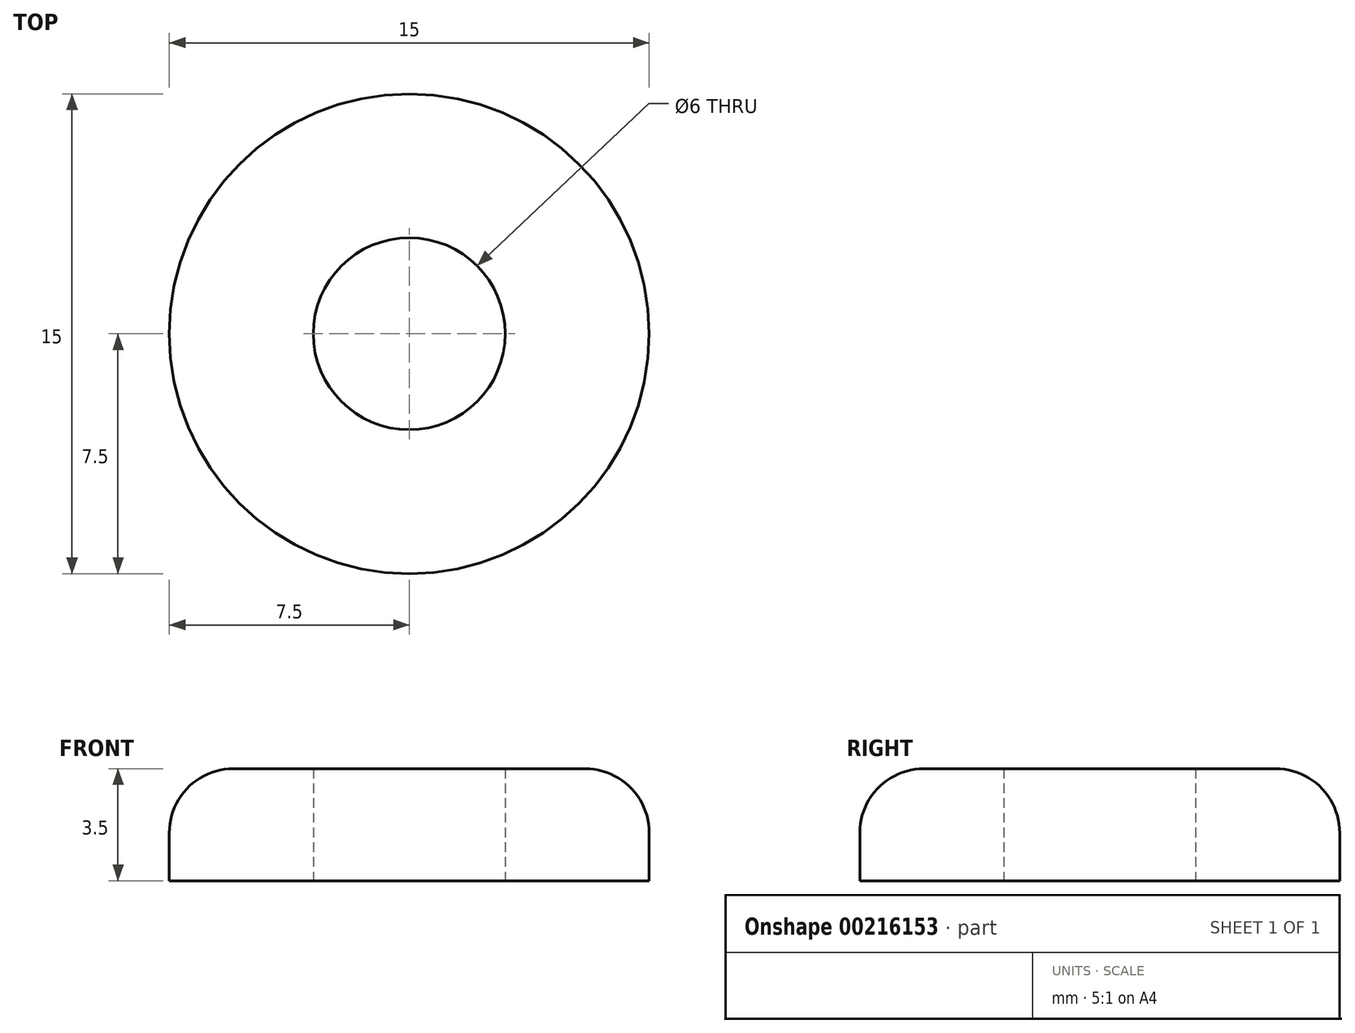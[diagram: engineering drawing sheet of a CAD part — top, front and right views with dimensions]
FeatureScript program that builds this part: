
annotation { "Feature Type Name" : "Feature", "Feature Type Description" : "" }
export const myFeature = defineFeature(function(context is Context, id is Id, definition is map)
    precondition{}
    {
        {
            var Q0;
            Q0=qCreatedBy(makeId("Front.planeOp"),FACE);
            var sketch = newSketch(context, id + "F0", { "sketchPlane" : qUnion([Q0])});
            skLineSegment(sketch, "E0", {"start": v(0, 0) * mm, "end": v(0, 9.1) * mm, "construction": true});
            skLineSegment(sketch, "E1.bottom", {"start": v(-3, 0) * mm, "end": v(-7.5, 0) * mm});
            skLineSegment(sketch, "E1.top", {"start": v(-3, 3.5) * mm, "end": v(-5.5, 3.5) * mm});
            skLineSegment(sketch, "E1.left", {"start": v(-3, 0) * mm, "end": v(-3, 3.5) * mm});
            skLineSegment(sketch, "E1.right", {"start": v(-7.5, 0) * mm, "end": v(-7.5, 1.5) * mm});
            skPoint(sketch, "E2.visualSharp", {"position": v(-7.5, 3.5) * mm});
            skArc(sketch, "E2.filletArc", {"start": v(-5.5, 3.5) * mm, "mid": v(-6.91, 2.91) * mm, "end": v(-7.5, 1.5) * mm});
            skSolve(sketch);
        }
        {
            var Q0;
            Q0=makeQuery(id+"F0.imprint","IMPRINT",FACE,{"disambiguationData":[TD([[makeQuery(id+"F0.imprint","IMPRINT",EDGE,{"derivedFrom":sQuery(id+"F0.wireOp",EDGE,"E1.bottom")}),-1.0]])]});
            var Q1;
            Q1=sQuery(id+"F0.wireOp",EDGE,"E0");
            revolve(context, id + "F1", {"entities" : qUnion([Q0]), "axis" : qUnion([Q1]), "revolveType" : RevolveType.FULL});
        }
    });
